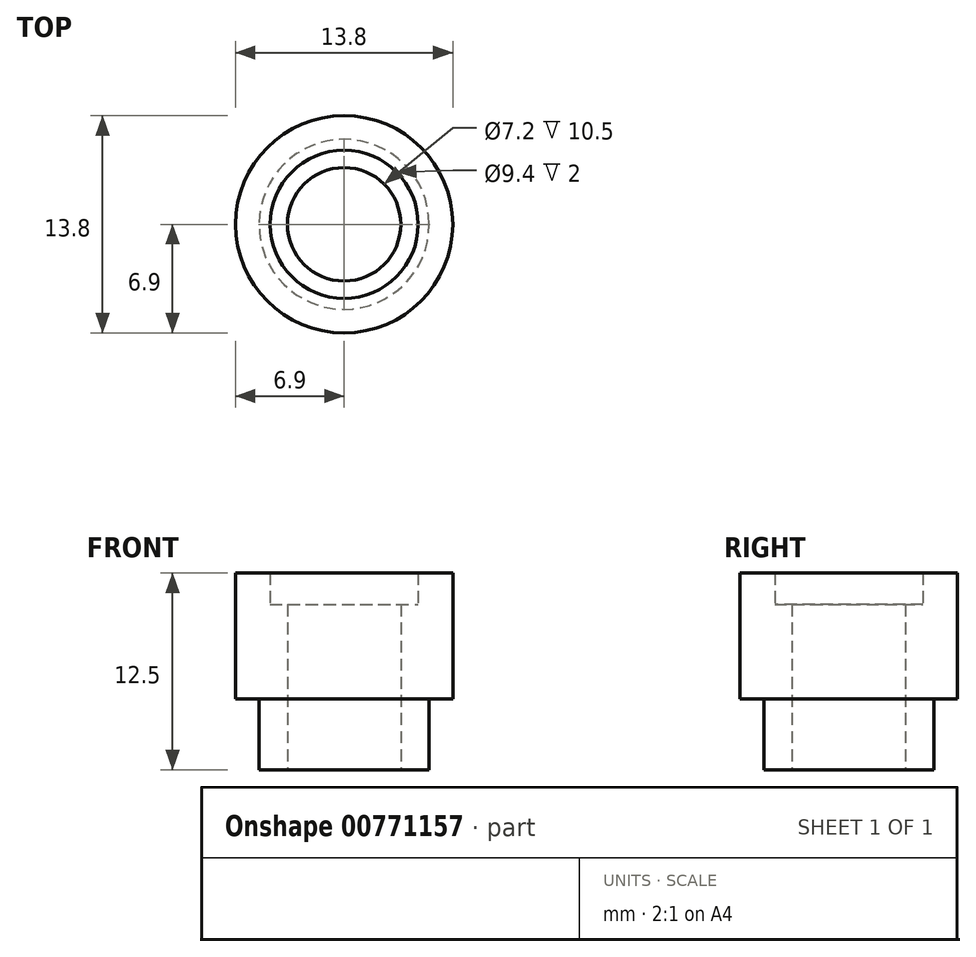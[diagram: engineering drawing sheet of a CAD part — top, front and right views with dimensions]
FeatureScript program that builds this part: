
annotation { "Feature Type Name" : "Feature", "Feature Type Description" : "" }
export const myFeature = defineFeature(function(context is Context, id is Id, definition is map)
    precondition{}
    {
        {
            var Q0;
            Q0=qCreatedBy(makeId("Front.planeOp"),FACE);
            var sketch = newSketch(context, id + "F0", { "sketchPlane" : qUnion([Q0])});
            skLineSegment(sketch, "E0", {"start": v(0, 0) * mm, "end": v(0, 15.61) * mm, "construction": true});
            skLineSegment(sketch, "E1", {"start": v(-3.6, 0) * mm, "end": v(-3.6, 10.5) * mm});
            skLineSegment(sketch, "E2", {"start": v(-3.6, 10.5) * mm, "end": v(-4.7, 10.5) * mm});
            skLineSegment(sketch, "E3", {"start": v(-4.7, 10.5) * mm, "end": v(-4.7, 12.5) * mm});
            skLineSegment(sketch, "E4", {"start": v(-4.7, 12.5) * mm, "end": v(-6.9, 12.5) * mm});
            skLineSegment(sketch, "E5", {"start": v(-6.9, 12.5) * mm, "end": v(-6.9, 4.5) * mm});
            skLineSegment(sketch, "E6", {"start": v(-6.9, 4.5) * mm, "end": v(-5.4, 4.5) * mm});
            skLineSegment(sketch, "E7", {"start": v(-5.4, 4.5) * mm, "end": v(-5.4, 0) * mm});
            skLineSegment(sketch, "E8", {"start": v(-5.4, 0) * mm, "end": v(-3.6, 0) * mm});
            skSolve(sketch);
        }
        {
            var Q0;
            Q0=makeQuery(id+"F0.imprint","IMPRINT",FACE,{"disambiguationData":[TD([[makeQuery(id+"F0.imprint","IMPRINT",EDGE,{"derivedFrom":sQuery(id+"F0.wireOp",EDGE,"E1")}),1.0]])]});
            var Q1;
            Q1=sQuery(id+"F0.wireOp",EDGE,"E0");
            revolve(context, id + "F1", {"surfaceOperationType" : NewSurfaceOperationType.NEW, "entities" : qUnion([Q0]), "axis" : qUnion([Q1]), "revolveType" : RevolveType.FULL});
        }
    });
